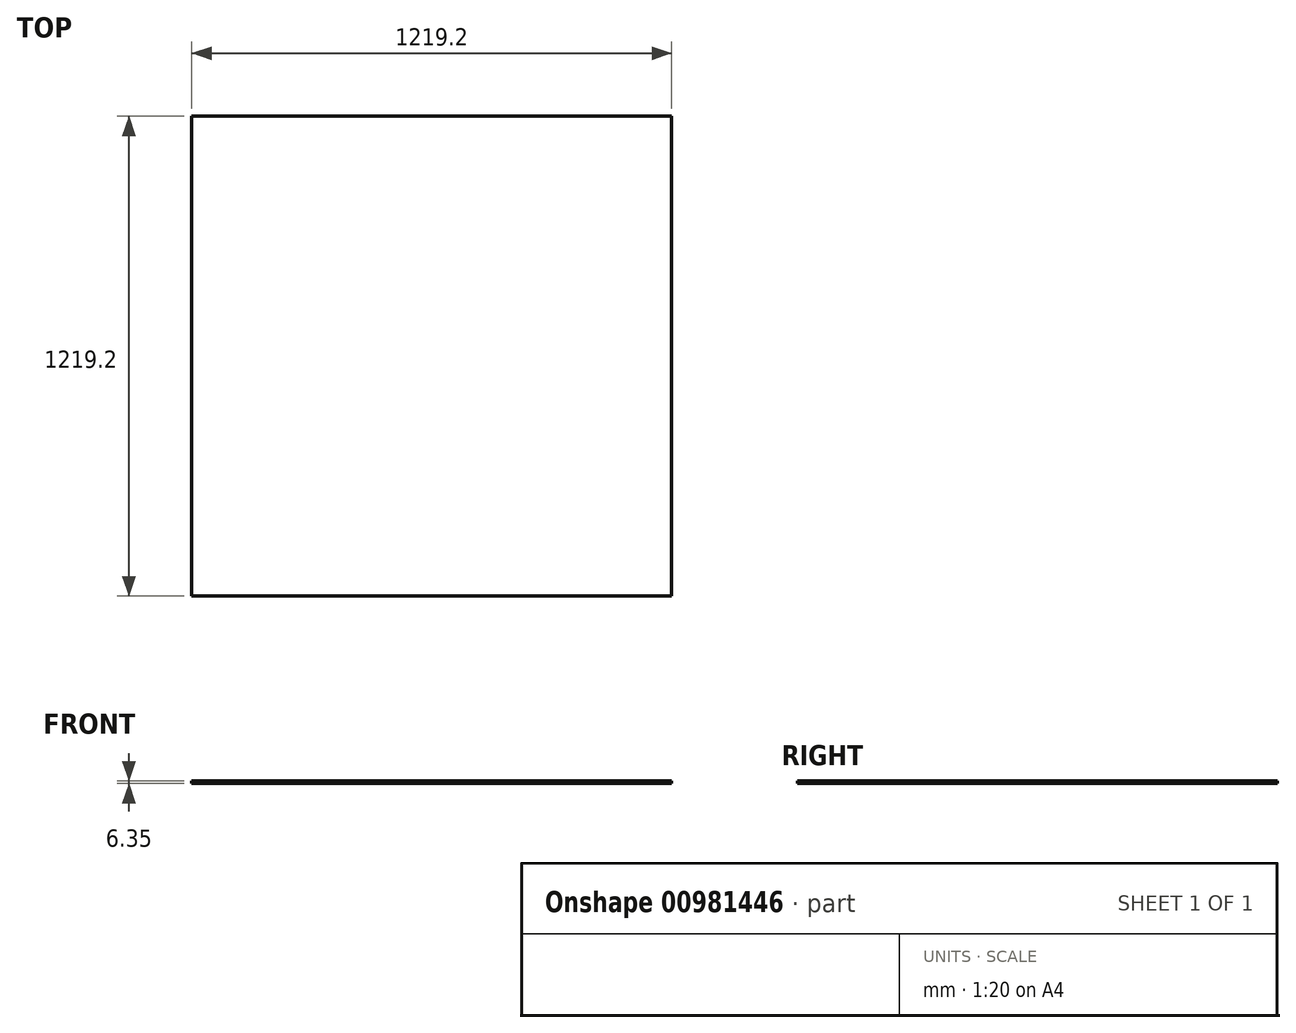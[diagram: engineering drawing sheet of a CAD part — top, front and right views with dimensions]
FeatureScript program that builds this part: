
annotation { "Feature Type Name" : "Feature", "Feature Type Description" : "" }
export const myFeature = defineFeature(function(context is Context, id is Id, definition is map)
    precondition{}
    {
        {
            var Q0;
            Q0=qCreatedBy(makeId("Top.planeOp"),FACE);
            var sketch = newSketch(context, id + "F0", { "sketchPlane" : qUnion([Q0])});
            skLineSegment(sketch, "E0.bottom", {"start": v(-609.6, 609.6) * mm, "end": v(609.6, 609.6) * mm});
            skLineSegment(sketch, "E0.top", {"start": v(-609.6, -609.6) * mm, "end": v(609.6, -609.6) * mm});
            skLineSegment(sketch, "E0.left", {"start": v(-609.6, 609.6) * mm, "end": v(-609.6, -609.6) * mm});
            skLineSegment(sketch, "E0.right", {"start": v(609.6, 609.6) * mm, "end": v(609.6, -609.6) * mm});
            skLineSegment(sketch, "E1", {"start": v(-609.6, 609.6) * mm, "end": v(609.6, -609.6) * mm});
            skLineSegment(sketch, "E2", {"start": v(0, 0) * mm, "end": v(0, 0) * mm});
            skSolve(sketch);
        }
        {
            var Q0;
            Q0 = qSketchRegion(id + "F0", true);
            extrude(context, id + "F1", {"entities" : qUnion([Q0]), "depth" : 6.35 * mm, "offsetDistance" : 25.4 * mm});
        }
    });
